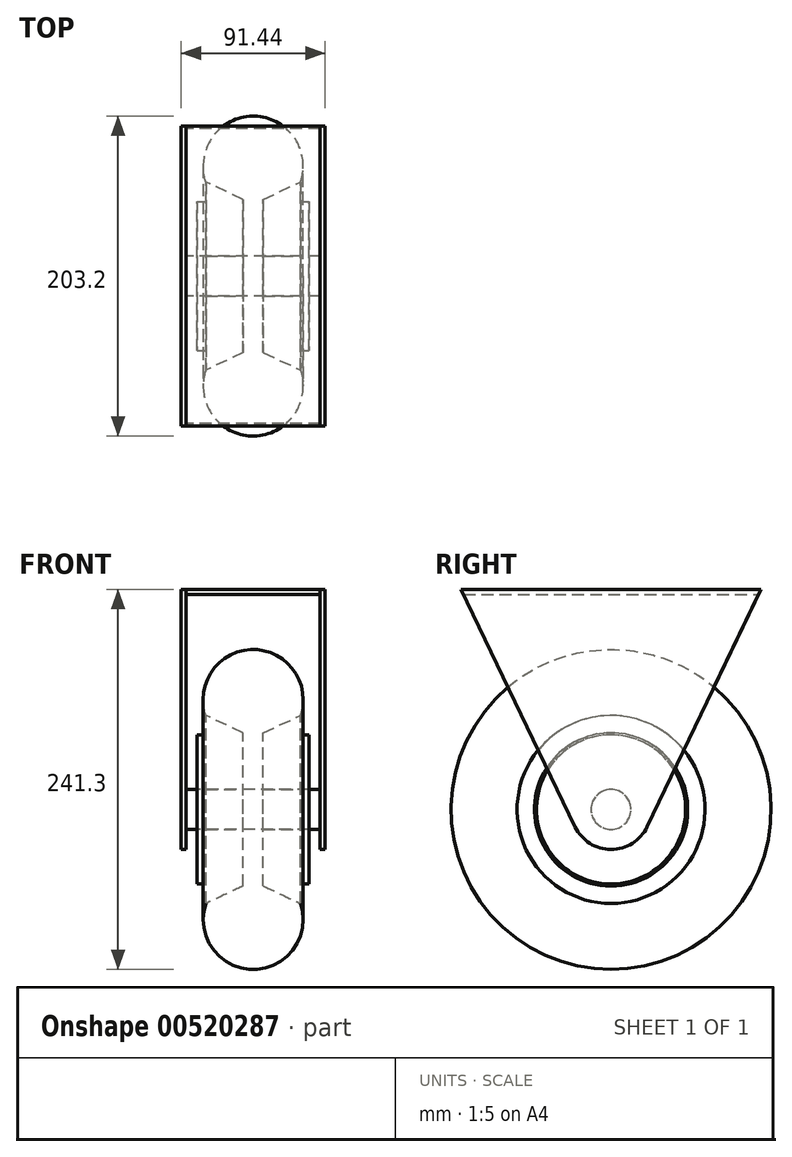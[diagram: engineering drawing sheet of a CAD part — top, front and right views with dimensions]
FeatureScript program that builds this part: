
annotation { "Feature Type Name" : "Feature", "Feature Type Description" : "" }
export const myFeature = defineFeature(function(context is Context, id is Id, definition is map)
    precondition{}
    {
        {
            var Q0;
            Q0=qCreatedBy(makeId("Front.planeOp"),FACE);
            var sketch = newSketch(context, id + "F0", { "sketchPlane" : qUnion([Q0])});
            skLineSegment(sketch, "E0", {"start": v(0, 101.6) * mm, "end": v(0, -101.6) * mm, "construction": true});
            skLineSegment(sketch, "E1", {"start": v(-30.08, 59.69) * mm, "end": v(-6.35, 48.68) * mm});
            skLineSegment(sketch, "E2", {"start": v(-6.35, 48.68) * mm, "end": v(-6.35, 12.7) * mm});
            skLineSegment(sketch, "E3", {"start": v(-6.35, 12.7) * mm, "end": v(-30.08, 12.7) * mm});
            skLineSegment(sketch, "E4", {"start": v(-30.08, 12.7) * mm, "end": v(-30.08, 47.37) * mm});
            skLineSegment(sketch, "E5", {"start": v(-30.08, 47.37) * mm, "end": v(-35.56, 47.37) * mm});
            skLineSegment(sketch, "E6", {"start": v(-35.56, 47.37) * mm, "end": v(-35.56, 0) * mm});
            skLineSegment(sketch, "E7", {"start": v(-35.56, 0) * mm, "end": v(0, 0) * mm});
            skArc(sketch, "E8", {"start": v(0, 101.6) * mm, "mid": v(-25.8, 88.36) * mm, "end": v(-30.08, 59.69) * mm});
            skLineSegment(sketch, "E9.MirrorCS", {"start": v(30.08, 59.69) * mm, "end": v(6.35, 48.68) * mm});
            skLineSegment(sketch, "E10.MirrorCS", {"start": v(35.56, 47.37) * mm, "end": v(35.56, 0) * mm});
            skLineSegment(sketch, "E11.MirrorCS", {"start": v(30.08, 47.37) * mm, "end": v(35.56, 47.37) * mm});
            skLineSegment(sketch, "E12.MirrorCS", {"start": v(6.35, 12.7) * mm, "end": v(30.08, 12.7) * mm});
            skLineSegment(sketch, "E13.MirrorCS", {"start": v(30.08, 12.7) * mm, "end": v(30.08, 47.37) * mm});
            skLineSegment(sketch, "E14.MirrorCS", {"start": v(6.35, 48.68) * mm, "end": v(6.35, 12.7) * mm});
            skArc(sketch, "E15.MirrorCS", {"start": v(0, 101.6) * mm, "mid": v(25.8, 88.36) * mm, "end": v(30.08, 59.69) * mm});
            skLineSegment(sketch, "E16.MirrorCS", {"start": v(35.56, 0) * mm, "end": v(0, 0) * mm});
            skSolve(sketch);
        }
        {
            var Q0;
            Q0=makeQuery(id+"F0.imprint","IMPRINT",FACE,{"disambiguationData":[TD([[makeQuery(id+"F0.imprint","IMPRINT",EDGE,{"derivedFrom":sQuery(id+"F0.wireOp",EDGE,"E1")}),1.0]])]});
            var Q1;
            Q1=sQuery(id+"F0.wireOp",EDGE,"E16.MirrorCS");
            revolve(context, id + "F1", {"entities" : qUnion([Q0]), "axis" : qUnion([Q1]), "revolveType" : RevolveType.FULL});
        }
        {
            var Q0;
            Q0=qCreatedBy(makeId("Right.planeOp"),FACE);
            cPlane(context, id + "F2", {"entities" : qUnion([Q0]), "cplaneType" : CPlaneType.OFFSET, "offset" : 45.72 * mm, "width" : 152.4 * mm, "height" : 152.4 * mm});
        }
        {
            var Q0;
            Q0=qCreatedBy(id+"F2.planeOp",FACE);
            var sketch = newSketch(context, id + "F3", { "sketchPlane" : qUnion([Q0])});
            skLineSegment(sketch, "E17", {"start": v(95.25, 139.7) * mm, "end": v(22.9, -11) * mm});
            skLineSegment(sketch, "E18", {"start": v(-22.9, -11) * mm, "end": v(-95.25, 139.7) * mm});
            skLineSegment(sketch, "E19", {"start": v(-95.25, 139.7) * mm, "end": v(95.25, 139.7) * mm});
            skLineSegment(sketch, "E20", {"start": v(0, 146.1) * mm, "end": v(0, -217.12) * mm, "construction": true});
            skPoint(sketch, "E21.visualSharp", {"position": v(0, -58.68) * mm});
            skArc(sketch, "E21.filletArc", {"start": v(-22.9, -11) * mm, "mid": v(0, -25.4) * mm, "end": v(22.9, -11) * mm});
            skSolve(sketch);
        }
        {
            var Q0;
            Q0=makeQuery(id+"F3.imprint","IMPRINT",FACE,{"disambiguationData":[TD([[makeQuery(id+"F3.imprint","IMPRINT",EDGE,{"derivedFrom":sQuery(id+"F3.wireOp",EDGE,"E17")}),-1.0]])]});
            extrude(context, id + "F4", {"entities" : qUnion([Q0]), "oppositeDirection" : true, "depth" : 3.17 * mm, "offsetDistance" : 25.4 * mm});
        }
        {
            var Q0;
            Q0=makeQuery(id+"F4.opExtrude","SWEPT_BODY",BODY,{"disambiguationData":[OSD([sQuery(id+"F3.wireOp",EDGE,"E17"),sQuery(id+"F3.wireOp",EDGE,"E18"),sQuery(id+"F3.wireOp",EDGE,"E19"),sQuery(id+"F3.wireOp",EDGE,"E21.filletArc")])]});
            var Q1;
            Q1=qCreatedBy(makeId("Right.planeOp"),FACE);
            mirror(context, id + "F5", {"entities" : qUnion([Q0]), "mirrorPlane" : qUnion([Q1])});
        }
        {
            var Q0;
            Q0=qCreatedBy(makeId("Right.planeOp"),FACE);
            var sketch = newSketch(context, id + "F6", { "sketchPlane" : qUnion([Q0])});
            skLineSegment(sketch, "E22.0", {"start": v(-95.25, 139.7) * mm, "end": v(95.25, 139.7) * mm});
            skLineSegment(sketch, "E23.0", {"start": v(-93.73, 136.53) * mm, "end": v(-95.25, 139.7) * mm});
            skLineSegment(sketch, "E24.0", {"start": v(95.25, 139.7) * mm, "end": v(93.73, 136.53) * mm});
            skLineSegment(sketch, "E25", {"start": v(-93.73, 136.53) * mm, "end": v(93.73, 136.53) * mm});
            skPoint(sketch, "E26.orphan", {"position": v(22.9, -11) * mm});
            skPoint(sketch, "E27.orphan", {"position": v(-22.9, -11) * mm});
            skSolve(sketch);
        }
        {
            var Q0;
            Q0=makeQuery(id+"F6.imprint","IMPRINT",FACE,{"disambiguationData":[TD([[makeQuery(id+"F6.imprint","IMPRINT",EDGE,{"derivedFrom":sQuery(id+"F6.wireOp",EDGE,"E22.0")}),-1.0]])]});
            extrude(context, id + "F7", {"entities" : qUnion([Q0]), "endBound" : BoundingType.UP_TO_NEXT, "depth" : 25.4 * mm, "offsetDistance" : 25.4 * mm, "hasSecondDirection" : true, "secondDirectionBound" : SecondDirectionBoundingType.UP_TO_NEXT, "secondDirectionOppositeDirection" : true, "secondDirectionDepth" : 25.4 * mm});
        }
        {
            var Q0;
            Q0=qCreatedBy(makeId("Right.planeOp"),FACE);
            var sketch = newSketch(context, id + "F8", { "sketchPlane" : qUnion([Q0])});
            skCircle(sketch, "E28", {"center": v(0, 0) * mm, "radius": 12.7 * mm});
            skSolve(sketch);
        }
        {
            var Q0;
            Q0=makeQuery(id+"F8.imprint","IMPRINT",FACE,{"disambiguationData":[TD([[makeQuery(id+"F8.imprint","IMPRINT",EDGE,{"derivedFrom":sQuery(id+"F8.wireOp",EDGE,"E28")}),1.0]])]});
            var Q1;
            Q1=sQuery(id+"F8.wireOp",EDGE,"E28");
            var Q2;
            Q2=makeQuery(id+"F4.opExtrude","CAP_FACE",FACE,{"disambiguationData":[OSD([sQuery(id+"F3.wireOp",EDGE,"E17"),sQuery(id+"F3.wireOp",EDGE,"E18"),sQuery(id+"F3.wireOp",EDGE,"E19"),sQuery(id+"F3.wireOp",EDGE,"E21.filletArc")])],"isStart":false});
            var Q3;
            Q3=makeQuery(id+"F5.opPattern","COPY",FACE,{"derivedFrom":makeQuery(id+"F4.opExtrude","CAP_FACE",FACE,{"disambiguationData":[OSD([sQuery(id+"F3.wireOp",EDGE,"E17"),sQuery(id+"F3.wireOp",EDGE,"E18"),sQuery(id+"F3.wireOp",EDGE,"E19"),sQuery(id+"F3.wireOp",EDGE,"E21.filletArc")])],"isStart":false}),"instanceName":"1"});
            extrude(context, id + "F9", {"entities" : qUnion([Q0]), "surfaceEntities" : qUnion([Q1]), "endBound" : BoundingType.UP_TO_SURFACE, "depth" : 25.4 * mm, "endBoundEntityFace" : qUnion([Q2]), "offsetDistance" : 25.4 * mm, "hasSecondDirection" : true, "secondDirectionBound" : SecondDirectionBoundingType.UP_TO_SURFACE, "secondDirectionOppositeDirection" : true, "secondDirectionDepth" : 25.4 * mm, "secondDirectionBoundEntityFace" : qUnion([Q3])});
        }
    });
